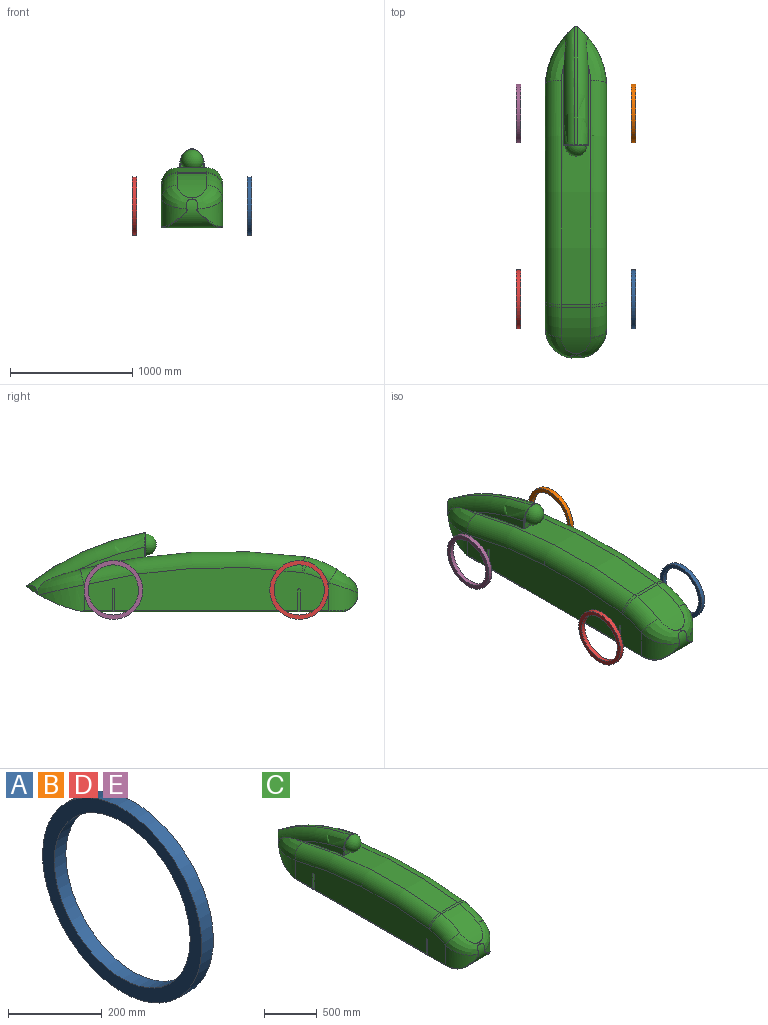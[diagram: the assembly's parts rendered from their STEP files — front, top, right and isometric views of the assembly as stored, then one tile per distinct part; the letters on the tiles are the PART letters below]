
ASSEMBLY  parts=5 mates=4
PART A: 4 faces, bbox 35x480x480 mm
  f0: cylinder r=205mm len=410mm, axis (-1,0,0), area 45081.9mm2, adj f2,f3
  f1: cylinder r=240mm len=480mm, axis (-1,0,0), area 52778.8mm2, adj f2,f3
  f2: plane 480x480mm, normal (1,0,0), area 48930.3mm2, adj f0,f1
  f3: plane 480x480mm, normal (-1,0,0), area 48930.3mm2, adj f0,f1
PART B: same geometry as A
PART C: 67 faces, bbox 539.6x2826.2x828.4 mm
  f0: plane 49.31x6.22mm, normal (0,-1,0), area 83.2mm2, adj f14,f35,f51,f54
  f1: plane 2000x354.51mm, normal (1,0,0), area 621262.9mm2, adj f11,f12,f17,f18,f19,f21,f22,f24
  f2: plane 2088.28x480mm, normal (0,0,-1), area 1000156.6mm2, adj f4,f8,f21,f22,f23,f25,f26,f27
  f3: cylinder r=635.32mm len=98.29mm, axis (0,0,-1), area 4000.4mm2, adj f4,f13,f53
  f4: cylinder r=1121.31mm len=496.86mm, axis (-1,0,0), area 173823.2mm2, adj f2,f3,f11,f13,f16,f30,f32,f34
  f5: cylinder r=4818.85mm len=1955.93mm, axis (-1,0,0), area 337810.1mm2, adj f6,f9,f10,f13,f15,f16,f17,f31
  f6: cylinder r=300mm len=240mm, axis (-1,0,0), area 5761.1mm2, adj f5,f7,f18,f39
  f7: cylinder r=792.57mm len=375.86mm, axis (-1,0,0), area 95058.9mm2, adj f6,f19,f20,f40,f41
  f8: cylinder r=150mm len=444.8mm, axis (-1,0,0), area 69728.2mm2, adj f2,f59,f60,f61,f62
  f9: plane 190x119.12mm, normal (0,-1,0), area 6306.3mm2, adj f5,f14,f15,f35,f36,f51
  f10: plane 549.44x188.07mm, normal (1,0,0), area 26697.7mm2, adj f5,f13,f15
  f11: cylinder r=635.32mm len=367.13mm, axis (0,0,-1), area 47992.1mm2, adj f1,f4,f16,f17,f65
  f12: cylinder r=240.2mm len=238.2mm, axis (0,0,-1), area 52999.2mm2, adj f1,f20,f58,f60
  f13: torus R=2073.72mm, axis (-1,0,0), area 140407.1mm2, adj f3,f4,f5,f10,f14,f16,f53
  f14: bspline ~135.02x99.8mm, area 1279.6mm2, adj f0,f9,f13,f15,f52,f54
  f15: cylinder r=5mm len=79.43mm, axis (0,0,1), area 621.2mm2, adj f5,f9,f10,f14
  f16: bspline ~432.63x261.5mm, area 64588.7mm2, adj f4,f5,f11,f13,f17
  f17: torus R=4688.85mm, axis (1,0,0), area 372943.7mm2, adj f1,f5,f11,f16,f18
  f18: torus R=170mm, axis (1,0,0), area 4130mm2, adj f1,f6,f17,f19
  f19: torus R=662.57mm, axis (1,0,0), area 50722.2mm2, adj f1,f7,f18,f20
  f20: bspline ~275.74x257.94mm, area 43860.7mm2, adj f7,f12,f19,f41,f62
  f21: plane 180x25mm, normal (0,1,0), area 4478.5mm2, adj f1,f2,f23,f24,f66
  f22: plane 180x25mm, normal (0,-1,0), area 4478.5mm2, adj f1,f2,f23,f24,f65
  f23: plane 190x20mm, normal (1,0,0), area 3757.1mm2, adj f2,f21,f22,f24
  f24: cylinder r=10mm len=25mm, axis (1,0,0), area 785.4mm2, adj f1,f21,f22,f23
  f25: plane 180x25mm, normal (0,-1,0), area 4478.5mm2, adj f1,f2,f27,f28,f66
  f26: plane 180x25mm, normal (0,1,0), area 4478.5mm2, adj f1,f2,f27,f28,f56
  f27: plane 190x20mm, normal (1,0,0), area 3757.1mm2, adj f2,f25,f26,f28
  f28: cylinder r=10mm len=25mm, axis (1,0,0), area 785.4mm2, adj f1,f25,f26,f27
  f29: plane 2000x354.51mm, normal (-1,0,0), area 621262.9mm2, adj f32,f33,f38,f39,f40,f42,f43,f45
  f30: cylinder r=635.32mm len=98.29mm, axis (0,0,-1), area 4000.2mm2, adj f4,f34,f53
  f31: plane 549.44x188.07mm, normal (-1,0,0), area 26697.7mm2, adj f5,f34,f36
  f32: cylinder r=635.32mm len=367.13mm, axis (0,0,-1), area 47992mm2, adj f4,f29,f37,f38,f64
  f33: cylinder r=240.2mm len=238.2mm, axis (0,0,-1), area 52998.5mm2, adj f29,f41,f57,f59
  f34: torus R=2073.72mm, axis (1,0,0), area 140403.8mm2, adj f4,f5,f30,f31,f35,f37,f53
  f35: bspline ~135.02x99.8mm, area 1279.6mm2, adj f0,f9,f34,f36,f50,f54
  f36: cylinder r=5mm len=79.43mm, axis (0,0,1), area 621.2mm2, adj f5,f9,f31,f35
  f37: bspline ~432.63x261.5mm, area 64588.7mm2, adj f4,f5,f32,f34,f38
  f38: torus R=4688.85mm, axis (-1,0,0), area 372943.7mm2, adj f5,f29,f32,f37,f39
  f39: torus R=170mm, axis (-1,0,0), area 4130mm2, adj f6,f29,f38,f40
  f40: torus R=662.57mm, axis (-1,0,0), area 50722.2mm2, adj f7,f29,f39,f41
  f41: bspline ~275.74x257.94mm, area 43860.4mm2, adj f7,f20,f33,f40,f61
  f42: plane 180x25mm, normal (0,1,0), area 4478.5mm2, adj f2,f29,f44,f45,f63
  f43: plane 180x25mm, normal (0,-1,0), area 4478.5mm2, adj f2,f29,f44,f45,f64
  f44: plane 190x20mm, normal (-1,0,0), area 3757.1mm2, adj f2,f42,f43,f45
  f45: cylinder r=10mm len=25mm, axis (-1,0,0), area 785.4mm2, adj f29,f42,f43,f44
  f46: plane 180x25mm, normal (0,-1,0), area 4478.5mm2, adj f2,f29,f48,f49,f63
  f47: plane 180x25mm, normal (0,1,0), area 4478.5mm2, adj f2,f29,f48,f49,f55
  f48: plane 190x20mm, normal (-1,0,0), area 3757.1mm2, adj f2,f46,f47,f49
  f49: cylinder r=10mm len=25mm, axis (-1,0,0), area 785.4mm2, adj f29,f46,f47,f48
  f50: plane 67.5x63.35mm, normal (0,1,0), area 203.1mm2, adj f35,f51
  f51: sphere r=90mm, area 50893.8mm2, adj f0,f9,f50,f52
  f52: plane 67.5x63.35mm, normal (0,1,0), area 203.1mm2, adj f14,f51
  f53: torus R=2140.81mm, axis (-1,0,0), area 30922.7mm2, adj f3,f4,f13,f30,f34,f54
  f54: bspline ~37.91x9.62mm, area 245.3mm2, adj f0,f14,f35,f53
  f55: cylinder r=10mm len=232mm, axis (0,-1,0), area 3644.2mm2, adj f2,f29,f47,f57
  f56: cylinder r=10mm len=232mm, axis (0,-1,0), area 3644.2mm2, adj f1,f2,f26,f58
  f57: torus R=230.2mm, axis (0,0,1), area 1462.6mm2, adj f2,f33,f55,f59
  f58: torus R=230.2mm, axis (0,0,1), area 1462.6mm2, adj f2,f12,f56,f60
  f59: bspline ~197.76x164.13mm, area 2700mm2, adj f8,f33,f57,f61
  f60: bspline ~197.76x164.13mm, area 2700mm2, adj f8,f12,f58,f62
  f61: bspline ~86.85x47.5mm, area 114.2mm2, adj f8,f41,f59,f62
  f62: bspline ~80.76x48.13mm, area 114.2mm2, adj f8,f20,f60,f61
  f63: cylinder r=10mm len=1498mm, axis (0,-1,0), area 23530.5mm2, adj f2,f29,f42,f46
  f64: cylinder r=10mm len=253.43mm, axis (0,-1,0), area 3796.9mm2, adj f2,f4,f29,f32,f43
  f65: cylinder r=10mm len=253.43mm, axis (0,-1,0), area 3796.9mm2, adj f1,f2,f4,f11,f22
  f66: cylinder r=10mm len=1498mm, axis (0,-1,0), area 23530.5mm2, adj f1,f2,f21,f25
PART D: same geometry as A
PART E: same geometry as A
PLACE A t=(221.37,-729.98,281.92)mm
PLACE B t=(221.37,788.02,281.92)mm
PLACE C t=(-231.13,528.02,101.92)mm fixed
PLACE D t=(-718.63,-729.98,281.92)mm
PLACE E t=(-718.63,788.02,281.92)mm
MATE fastened A.f0 <-> C.f28  axis (-1,0,0) through (221.37,-729.98,281.92)mm
MATE fastened D.f0 <-> C.f28  axis (1,0,0) through (-683.63,-729.98,281.92)mm
MATE fastened B.f0 <-> C.f24  axis (-1,0,0) through (221.37,788.02,281.92)mm
MATE fastened E.f0 <-> C.f24  axis (1,0,0) through (-683.63,788.02,281.92)mm
